# Revit family: Tub_Spout-American_Standard-Studio_S-8888.31X_Series
name_source: partatom
category: Plumbing Fixtures
units: mm (PartAtom-declared; Revit-internal decimal feet)

## family parameters
Cut with Voids When Loaded = No
Host = Face
OmniClass Number = 23.45.05.14.17
OmniClass Title = Showers
Part Type = Normal
Room Calculation Point = No
Round Connector Dimension = Use Diameter
Shared = Yes

## types (4) — shared parameters
Assembly Code = D2020300
CW Connection = Yes
CWFU = 3
Default Elevation = 21"
Finish = Metal-American Standard-002-Polished Chrome
HW Connection = Yes
HWFU = 3
Installation Type = Wall Mounted
Length = 6 1/8"
Manufacturer = American Standard
Material = Metal-American Standard-002-Polished Chrome
Price = Prices may vary. Please consult Manufacturer Representative for most up-to-date price list.
Product Page URL = https://www.americanstandard-us.com
URL = https://www.americanstandard-us.com
Vent Connection = No
WFU = 4
Warranty Information = Limited Lifetime Function and Finish Warranty
Waste Connection = Yes
Water Connection Diameter = 1/2"
Water Connection Radius = 1/4"
Width = 2 3/4"

## per-type parameters (varying)
| type | Description | Pop-up handle |
| 8888.316 | Slip-On Non-Diverter Tub Spout | No |
| 8888.317 | Non-Diverter 1/2 IPS Tub Spout | No |
| 8888.318 | Slip-On-Diverter Tub Spout | Yes |
| 8888.319 | Diverter 1/2 IPS Tub Spout | Yes |

note: column(s) folded — value = type name in every type: Model

## geometry (parser evidence)
native form markers: Sweep x3
no freeform markers — native parametric forms only
